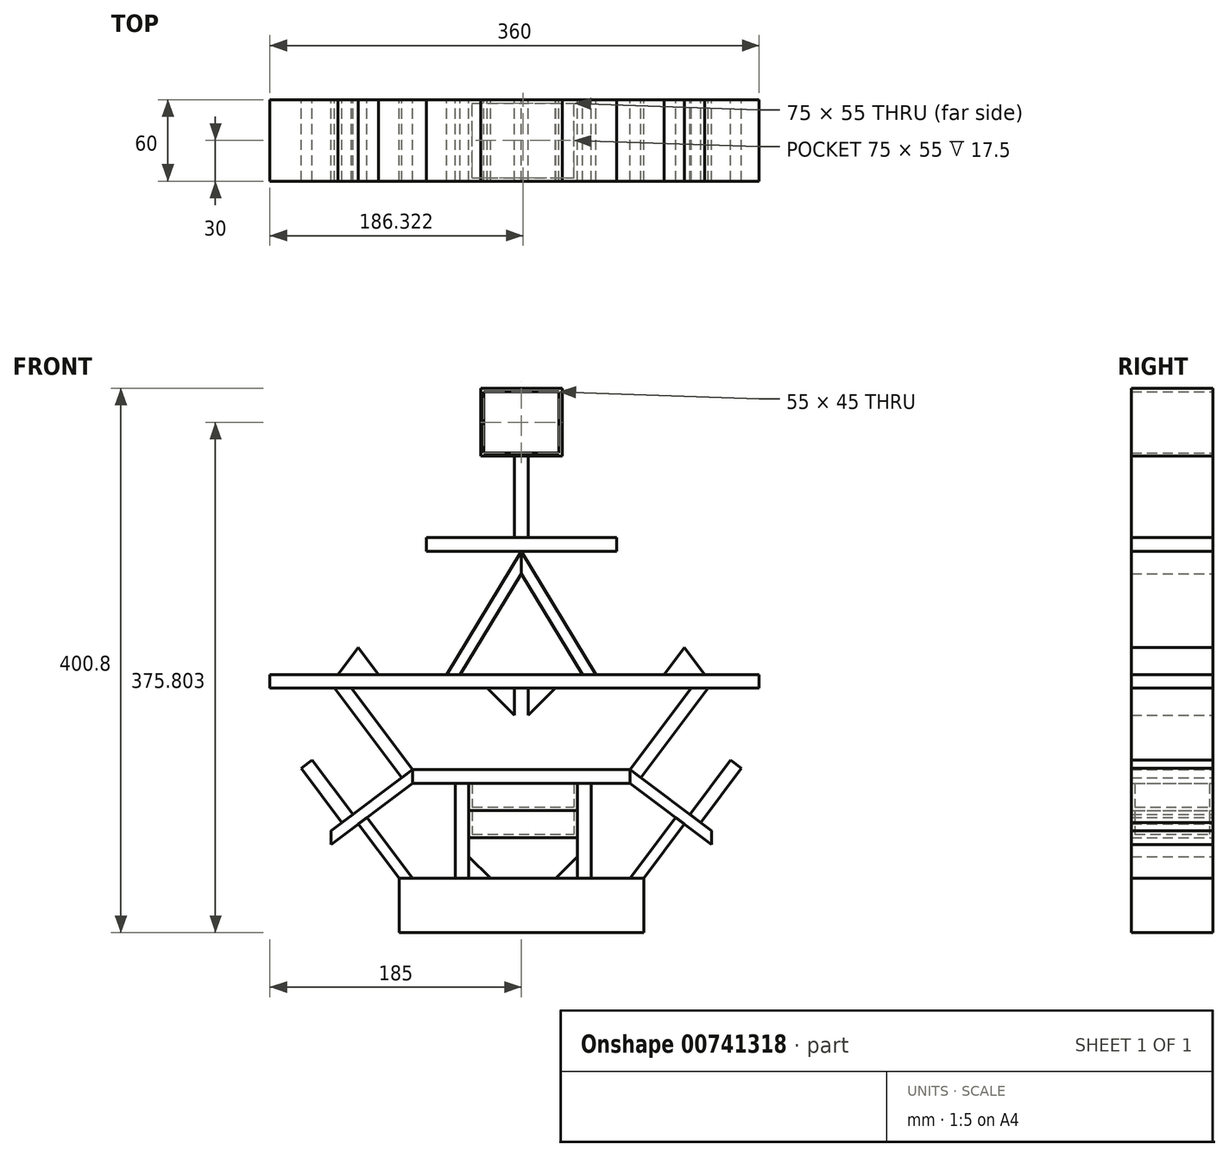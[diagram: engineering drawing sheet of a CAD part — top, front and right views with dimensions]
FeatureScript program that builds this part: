
annotation { "Feature Type Name" : "Feature", "Feature Type Description" : "" }
export const myFeature = defineFeature(function(context is Context, id is Id, definition is map)
    precondition{}
    {
        {
            var Q0;
            Q0=qCreatedBy(makeId("Top.planeOp"),FACE);
            var sketch = newSketch(context, id + "F0", { "sketchPlane" : qUnion([Q0])});
            skLineSegment(sketch, "E0.bottom", {"start": v(90, -30) * mm, "end": v(-90, -30) * mm});
            skLineSegment(sketch, "E0.top", {"start": v(90, 30) * mm, "end": v(-90, 30) * mm});
            skLineSegment(sketch, "E0.left", {"start": v(90, -30) * mm, "end": v(90, 30) * mm});
            skLineSegment(sketch, "E0.right", {"start": v(-90, -30) * mm, "end": v(-90, 30) * mm});
            skPoint(sketch, "E0.middle", {"position": v(0, 0) * mm});
            skSolve(sketch);
        }
        {
            var Q0;
            Q0 = qSketchRegion(id + "F0", true);
            extrude(context, id + "F1", {"entities" : qUnion([Q0]), "oppositeDirection" : true, "depth" : 40 * mm, "offsetDistance" : 25 * mm});
        }
        {
            var Q0;
            Q0=makeQuery(id+"F1.opExtrude","SWEPT_FACE",FACE,{"disambiguationData":[OSD([sQuery(id+"F0.wireOp",EDGE,"E0.top")])]});
            var sketch = newSketch(context, id + "F2", { "sketchPlane" : qUnion([Q0])});
            skLineSegment(sketch, "E1", {"start": v(90, 0) * mm, "end": v(80, 0) * mm});
            skLineSegment(sketch, "E2", {"start": v(80, 0) * mm, "end": v(113.6, 44.8) * mm});
            skLineSegment(sketch, "E3", {"start": v(120, 40) * mm, "end": v(90, 0) * mm});
            skLineSegment(sketch, "E4.bottom", {"start": v(38.68, 70) * mm, "end": v(-41.32, 70) * mm});
            skLineSegment(sketch, "E4.top", {"start": v(38.68, 0) * mm, "end": v(-41.32, 0) * mm});
            skLineSegment(sketch, "E4.left", {"start": v(38.68, 70) * mm, "end": v(38.68, 0) * mm});
            skLineSegment(sketch, "E4.right", {"start": v(-41.32, 70) * mm, "end": v(-41.32, 0) * mm});
            skLineSegment(sketch, "E5", {"start": v(38.68, 30) * mm, "end": v(-41.32, 30) * mm});
            skLineSegment(sketch, "E6", {"start": v(38.68, 50) * mm, "end": v(-41.32, 50) * mm});
            skLineSegment(sketch, "E7", {"start": v(-41.32, 16) * mm, "end": v(-25.32, 0) * mm});
            skLineSegment(sketch, "E8", {"start": v(38.68, 70) * mm, "end": v(48.68, 70) * mm});
            skLineSegment(sketch, "E9", {"start": v(48.68, 70) * mm, "end": v(48.68, 0) * mm});
            skLineSegment(sketch, "E10", {"start": v(-41.32, 70) * mm, "end": v(-51.32, 70) * mm});
            skLineSegment(sketch, "E11", {"start": v(-51.32, 70) * mm, "end": v(-51.32, 0) * mm});
            skLineSegment(sketch, "E12", {"start": v(38.68, 16) * mm, "end": v(22.68, 0) * mm});
            skLineSegment(sketch, "E13", {"start": v(113.6, 44.8) * mm, "end": v(120, 40) * mm});
            skLineSegment(sketch, "E14", {"start": v(80, 70) * mm, "end": v(-80, 70) * mm});
            skLineSegment(sketch, "E15", {"start": v(-80, 70) * mm, "end": v(-80, 80) * mm});
            skLineSegment(sketch, "E16", {"start": v(-80, 80) * mm, "end": v(80, 80) * mm});
            skLineSegment(sketch, "E17", {"start": v(80, 80) * mm, "end": v(80, 70) * mm});
            skLineSegment(sketch, "E18", {"start": v(5, 80) * mm, "end": v(-5, 80) * mm});
            skLineSegment(sketch, "E19", {"start": v(-5, 80) * mm, "end": v(-5, 140) * mm});
            skLineSegment(sketch, "E20", {"start": v(-5, 140) * mm, "end": v(5, 140) * mm});
            skLineSegment(sketch, "E21", {"start": v(5, 140) * mm, "end": v(5, 80) * mm});
            skLineSegment(sketch, "E22", {"start": v(185, 140) * mm, "end": v(-175, 140) * mm});
            skLineSegment(sketch, "E23", {"start": v(-175, 140) * mm, "end": v(-175, 150) * mm});
            skLineSegment(sketch, "E24", {"start": v(-175, 150) * mm, "end": v(185, 150) * mm});
            skLineSegment(sketch, "E25", {"start": v(185, 150) * mm, "end": v(185, 140) * mm});
            skLineSegment(sketch, "E26", {"start": v(80, 80) * mm, "end": v(140, 35) * mm});
            skLineSegment(sketch, "E27", {"start": v(140, 35) * mm, "end": v(140, 25) * mm});
            skLineSegment(sketch, "E28", {"start": v(140, 25) * mm, "end": v(80, 70) * mm});
            skLineSegment(sketch, "E29", {"start": v(124, 47) * mm, "end": v(154, 87) * mm});
            skLineSegment(sketch, "E30", {"start": v(154, 87) * mm, "end": v(162, 81) * mm});
            skLineSegment(sketch, "E31", {"start": v(162, 81) * mm, "end": v(132, 41) * mm});
            skLineSegment(sketch, "E32", {"start": v(80, 80) * mm, "end": v(125, 140) * mm});
            skLineSegment(sketch, "E33", {"start": v(125, 140) * mm, "end": v(137.5, 140) * mm});
            skLineSegment(sketch, "E34", {"start": v(137.5, 140) * mm, "end": v(88, 74) * mm});
            skLineSegment(sketch, "E35", {"start": v(88, 74) * mm, "end": v(80, 80) * mm});
            skLineSegment(sketch, "E36", {"start": v(25, 140) * mm, "end": v(5, 120) * mm});
            skLineSegment(sketch, "E37", {"start": v(25, 140) * mm, "end": v(5, 140) * mm});
            skLineSegment(sketch, "E38", {"start": v(5, 120) * mm, "end": v(5, 140) * mm});
            skLineSegment(sketch, "E39", {"start": v(175, 150) * mm, "end": v(165, 150) * mm});
            skLineSegment(sketch, "E40", {"start": v(165, 150) * mm, "end": v(165, 160) * mm});
            skLineSegment(sketch, "E41", {"start": v(165, 160) * mm, "end": v(175, 160) * mm});
            skLineSegment(sketch, "E42", {"start": v(175, 160) * mm, "end": v(175, 150) * mm});
            skLineSegment(sketch, "E43", {"start": v(135, 150) * mm, "end": v(120, 170) * mm});
            skLineSegment(sketch, "E44", {"start": v(120, 170) * mm, "end": v(105, 150) * mm});
            skLineSegment(sketch, "E45", {"start": v(105, 150) * mm, "end": v(135, 150) * mm});
            skLineSegment(sketch, "E46", {"start": v(173.1, 240.8) * mm, "end": v(105, 150) * mm});
            skLineSegment(sketch, "E47", {"start": v(105, 150) * mm, "end": v(95, 150) * mm});
            skLineSegment(sketch, "E48", {"start": v(55, 150) * mm, "end": v(0, 240.8) * mm});
            skLineSegment(sketch, "E49", {"start": v(0, 240.8) * mm, "end": v(0, 224.3) * mm});
            skLineSegment(sketch, "E50", {"start": v(0, 224.3) * mm, "end": v(45, 150) * mm});
            skLineSegment(sketch, "E51", {"start": v(45, 150) * mm, "end": v(55, 150) * mm});
            skLineSegment(sketch, "E52", {"start": v(120, 150) * mm, "end": v(135, 150) * mm});
            skLineSegment(sketch, "E53", {"start": v(173.1, 240.8) * mm, "end": v(163.1, 240.8) * mm});
            skLineSegment(sketch, "E54", {"start": v(163.1, 240.8) * mm, "end": v(95, 150) * mm});
            skLineSegment(sketch, "E55", {"start": v(0, 224.3) * mm, "end": v(0, 240.8) * mm});
            skLineSegment(sketch, "E56", {"start": v(70, 240.8) * mm, "end": v(-70, 240.8) * mm});
            skLineSegment(sketch, "E57", {"start": v(-70, 240.8) * mm, "end": v(-70, 250.8) * mm});
            skLineSegment(sketch, "E58", {"start": v(-70, 250.8) * mm, "end": v(70, 250.8) * mm});
            skLineSegment(sketch, "E59", {"start": v(70, 250.8) * mm, "end": v(70, 240.8) * mm});
            skLineSegment(sketch, "E60", {"start": v(0, 240.8) * mm, "end": v(10, 224.3) * mm});
            skLineSegment(sketch, "E61", {"start": v(30, 240.8) * mm, "end": v(0, 240.8) * mm});
            skLineSegment(sketch, "E62", {"start": v(30, 240.8) * mm, "end": v(15, 216.67) * mm});
            skLineSegment(sketch, "E63", {"start": v(15, 216.67) * mm, "end": v(0, 240.8) * mm});
            skLineSegment(sketch, "E64", {"start": v(0, 224.3) * mm, "end": v(10.42, 207.09) * mm});
            skLineSegment(sketch, "E65", {"start": v(10.42, 207.09) * mm, "end": v(-10.75, 207.09) * mm});
            skLineSegment(sketch, "E66", {"start": v(-10.75, 207.09) * mm, "end": v(0, 224.3) * mm});
            skLineSegment(sketch, "E67", {"start": v(70, 250.8) * mm, "end": v(60, 250.8) * mm});
            skLineSegment(sketch, "E68", {"start": v(60, 250.8) * mm, "end": v(60, 290.8) * mm});
            skLineSegment(sketch, "E69", {"start": v(60, 290.8) * mm, "end": v(70, 290.8) * mm});
            skLineSegment(sketch, "E70", {"start": v(70, 290.8) * mm, "end": v(70, 250.8) * mm});
            skLineSegment(sketch, "E71", {"start": v(15, 250.8) * mm, "end": v(0, 250.8) * mm});
            skLineSegment(sketch, "E72", {"start": v(5, 310.8) * mm, "end": v(-5, 310.8) * mm});
            skLineSegment(sketch, "E73", {"start": v(-5, 310.8) * mm, "end": v(-5, 250.8) * mm});
            skLineSegment(sketch, "E74", {"start": v(5, 310.8) * mm, "end": v(5, 250.8) * mm});
            skLineSegment(sketch, "E75", {"start": v(5, 250.8) * mm, "end": v(-5, 250.8) * mm});
            skLineSegment(sketch, "E76", {"start": v(-30, 310.8) * mm, "end": v(-30, 360.8) * mm});
            skLineSegment(sketch, "E77", {"start": v(-30, 360.8) * mm, "end": v(30, 360.8) * mm});
            skLineSegment(sketch, "E78", {"start": v(30, 360.8) * mm, "end": v(30, 310.8) * mm});
            skLineSegment(sketch, "E79", {"start": v(30, 310.8) * mm, "end": v(-30, 310.8) * mm});
            skSolve(sketch);
        }
        {
            var Q0;
            Q0=makeQuery(id+"F2.imprint","IMPRINT",FACE,{"disambiguationData":[TD([[makeQuery(id+"F2.imprint","IMPRINT",EDGE,{"derivedFrom":sQuery(id+"F2.wireOp",EDGE,"E1")}),1.0]])]});
            var Q1;
            {var subQ0=sQuery(id+"F2.wireOp",EDGE,"E29");Q1=makeQuery(id+"F2.imprint","IMPRINT",FACE,{"disambiguationData":[TD([[makeQuery(id+"F2.imprint","IMPRINT",EDGE,{"derivedFrom":subQ0}),-1.0]])]});}
            var Q2;
            Q2=makeQuery(id+"F2.imprint","IMPRINT",FACE,{"disambiguationData":[TD([[makeQuery(id+"F2.imprint","IMPRINT",EDGE,{"derivedFrom":sQuery(id+"F2.wireOp",EDGE,"E32")}),-1.0]])]});
            var Q3;
            Q3=makeQuery(id+"F2.imprint","IMPRINT",FACE,{"disambiguationData":[TD([[makeQuery(id+"F2.imprint","IMPRINT",EDGE,{"derivedFrom":sQuery(id+"F2.wireOp",EDGE,"E36")}),-1.0]])]});
            var Q4;
            Q4=makeQuery(id+"F2.imprint","IMPRINT",FACE,{"disambiguationData":[TD([[makeQuery(id+"F2.imprint","IMPRINT",EDGE,{"derivedFrom":sQuery(id+"F2.wireOp",EDGE,"E43")}),1.0]])]});
            var Q5;
            Q5=makeQuery(id+"F2.imprint","IMPRINT",FACE,{"disambiguationData":[TD([[makeQuery(id+"F2.imprint","IMPRINT",EDGE,{"derivedFrom":sQuery(id+"F2.wireOp",EDGE,"E39")}),-1.0]])]});
            var Q6;
            Q6=makeQuery(id+"F2.imprint","IMPRINT",FACE,{"disambiguationData":[TD([[makeQuery(id+"F2.imprint","IMPRINT",EDGE,{"derivedFrom":sQuery(id+"F2.wireOp",EDGE,"E48")}),1.0]])]});
            var Q7;
            Q7=sQuery(id+"F2.wireOp",EDGE,"y02XFMRa-m6S5-seBa-FdlV-A9luelnOKwn0");
            var Q8;
            Q8=sQuery(id+"F2.wireOp",EDGE,"E3");
            var Q9;
            Q9=sQuery(id+"F2.wireOp",EDGE,"E2");
            var Q10;
            Q10=sQuery(id+"F2.wireOp",EDGE,"E1");
            extrude(context, id + "F3", {"entities" : qUnion([Q0, Q1, Q2, Q3, Q4, Q5, Q6]), "surfaceEntities" : qUnion([Q7, Q8, Q9, Q10]), "oppositeDirection" : true, "depth" : 60 * mm, "offsetDistance" : 25 * mm});
        }
        {
            var Q0;
            Q0=makeQuery(id+"F3.opExtrude","SWEPT_BODY",BODY,{"disambiguationData":[OSD([sQuery(id+"F2.wireOp",EDGE,"E2")])]});
            var Q1;
            Q1=makeQuery(id+"F3.opExtrude","SWEPT_BODY",BODY,{"disambiguationData":[OSD([sQuery(id+"F2.wireOp",EDGE,"E26"),sQuery(id+"F2.wireOp",EDGE,"E29"),sQuery(id+"F2.wireOp",EDGE,"E30"),sQuery(id+"F2.wireOp",EDGE,"E31")])]});
            var Q2;
            Q2=makeQuery(id+"F3.opExtrude","SWEPT_BODY",BODY,{"disambiguationData":[OSD([sQuery(id+"F2.wireOp",EDGE,"E32"),sQuery(id+"F2.wireOp",EDGE,"E33"),sQuery(id+"F2.wireOp",EDGE,"E34"),sQuery(id+"F2.wireOp",EDGE,"E35")])]});
            var Q3;
            Q3=makeQuery(id+"F3.opExtrude","SWEPT_BODY",BODY,{"disambiguationData":[OSD([sQuery(id+"F2.wireOp",EDGE,"E36"),sQuery(id+"F2.wireOp",EDGE,"E38"),sQuery(id+"F2.wireOp",EDGE,"E37")])]});
            var Q4;
            Q4=makeQuery(id+"F3.opExtrude","SWEPT_BODY",BODY,{"disambiguationData":[OSD([sQuery(id+"F2.wireOp",EDGE,"E39"),sQuery(id+"F2.wireOp",EDGE,"E40"),sQuery(id+"F2.wireOp",EDGE,"E41"),sQuery(id+"F2.wireOp",EDGE,"E42")])]});
            var Q5;
            Q5=makeQuery(id+"F3.opExtrude","SWEPT_BODY",BODY,{"disambiguationData":[OSD([sQuery(id+"F2.wireOp",EDGE,"E43"),sQuery(id+"F2.wireOp",EDGE,"E44"),sQuery(id+"F2.wireOp",EDGE,"E45"),sQuery(id+"F2.wireOp",EDGE,"E52")])]});
            var Q6;
            Q6=makeQuery(id+"F3.opExtrude","SWEPT_BODY",BODY,{"disambiguationData":[OSD([sQuery(id+"F2.wireOp",EDGE,"E48"),sQuery(id+"F2.wireOp",EDGE,"E50"),sQuery(id+"F2.wireOp",EDGE,"E51"),sQuery(id+"F2.wireOp",EDGE,"E55")])]});
            var Q7;
            Q7=qCreatedBy(makeId("Right.planeOp"),FACE);
            mirror(context, id + "F4", {"entities" : qUnion([Q0, Q1, Q2, Q3, Q4, Q5, Q6]), "mirrorPlane" : qUnion([Q7])});
        }
        {
            var Q0;
            {var subQ0=sQuery(id+"F2.wireOp",EDGE,"E5");Q0=makeQuery(id+"F2.imprint","IMPRINT",FACE,{"disambiguationData":[TD([[makeQuery(id+"F2.imprint","IMPRINT",EDGE,{"derivedFrom":subQ0}),-1.0]])]});}
            extrude(context, id + "F5", {"entities" : qUnion([Q0]), "oppositeDirection" : true, "depth" : 60 * mm, "offsetDistance" : 25 * mm});
        }
        {
            var Q0;
            Q0=makeQuery(id+"F5.opExtrude","SWEPT_FACE",FACE,{"disambiguationData":[OSD([sQuery(id+"F2.wireOp",EDGE,"E6")])]});
            shell(context, id + "F6", {"entities" : qUnion([Q0]), "thickness" : 2.5 * mm});
        }
        {
            var Q0;
            {var subQ0=sQuery(id+"F2.wireOp",EDGE,"E4.bottom");Q0=makeQuery(id+"F2.imprint","IMPRINT",FACE,{"disambiguationData":[TD([[makeQuery(id+"F2.imprint","IMPRINT",EDGE,{"derivedFrom":subQ0}),1.0]])]});}
            var Q1;
            {var subQ3=sQuery(id+"F2.wireOp",EDGE,"E6");Q1=makeQuery(id+"F2.imprint","IMPRINT",FACE,{"disambiguationData":[TD([[makeQuery(id+"F2.imprint","IMPRINT",EDGE,{"derivedFrom":subQ3}),-1.0]])]});}
            var Q2;
            Q2=makeQuery(id+"F2.imprint","IMPRINT",FACE,{"disambiguationData":[TD([[makeQuery(id+"F2.imprint","IMPRINT",EDGE,{"derivedFrom":sQuery(id+"F2.wireOp",EDGE,"E64")}),-1.0]])]});
            extrude(context, id + "F7", {"entities" : qUnion([Q0, Q1, Q2]), "oppositeDirection" : true, "depth" : 60 * mm, "offsetDistance" : 25 * mm});
        }
        {
            var Q0;
            Q0=makeQuery(id+"F7.opExtrude","SWEPT_FACE",FACE,{"disambiguationData":[OSD([sQuery(id+"F2.wireOp",EDGE,"E4.bottom")])]});
            var Q1;
            Q1=makeQuery(id+"F7.opExtrude","SWEPT_FACE",FACE,{"disambiguationData":[OSD([sQuery(id+"F2.wireOp",EDGE,"E14")])]});
            shell(context, id + "F8", {"entities" : qUnion([Q0, Q1]), "thickness" : 2.5 * mm});
        }
        {
            var Q0;
            {var subQ8=sQuery(id+"F2.wireOp",EDGE,"E9");Q0=makeQuery(id+"F2.imprint","IMPRINT",FACE,{"disambiguationData":[TD([[makeQuery(id+"F2.imprint","IMPRINT",EDGE,{"derivedFrom":subQ8}),-1.0]])]});}
            var Q1;
            {var subQ6=sQuery(id+"F2.wireOp",EDGE,"E11");Q1=makeQuery(id+"F2.imprint","IMPRINT",FACE,{"disambiguationData":[TD([[makeQuery(id+"F2.imprint","IMPRINT",EDGE,{"derivedFrom":subQ6}),1.0]])]});}
            var Q2;
            Q2=makeQuery(id+"F2.imprint","IMPRINT",FACE,{"disambiguationData":[TD([[makeQuery(id+"F2.imprint","IMPRINT",EDGE,{"derivedFrom":sQuery(id+"F2.wireOp",EDGE,"E18")}),-1.0]])]});
            extrude(context, id + "F9", {"entities" : qUnion([Q0, Q1, Q2]), "oppositeDirection" : true, "depth" : 60 * mm, "offsetDistance" : 25 * mm});
        }
        {
            var Q0;
            {var subQ3=sQuery(id+"F2.wireOp",EDGE,"E7");Q0=makeQuery(id+"F2.imprint","IMPRINT",FACE,{"disambiguationData":[TD([[makeQuery(id+"F2.imprint","IMPRINT",EDGE,{"derivedFrom":subQ3}),-1.0]])]});}
            var Q1;
            {var subQ3=sQuery(id+"F2.wireOp",EDGE,"E12");Q1=makeQuery(id+"F2.imprint","IMPRINT",FACE,{"disambiguationData":[TD([[makeQuery(id+"F2.imprint","IMPRINT",EDGE,{"derivedFrom":subQ3}),1.0]])]});}
            var Q2;
            {var subQ0=sQuery(id+"F2.wireOp",EDGE,"E23");Q2=makeQuery(id+"F2.imprint","IMPRINT",FACE,{"disambiguationData":[TD([[makeQuery(id+"F2.imprint","IMPRINT",EDGE,{"derivedFrom":subQ0}),-1.0]])]});}
            var Q3;
            {var subQ6=sQuery(id+"F2.wireOp",EDGE,"E15");Q3=makeQuery(id+"F2.imprint","IMPRINT",FACE,{"disambiguationData":[TD([[makeQuery(id+"F2.imprint","IMPRINT",EDGE,{"derivedFrom":subQ6}),-1.0]])]});}
            var Q4;
            Q4=makeQuery(id+"F2.imprint","IMPRINT",FACE,{"disambiguationData":[TD([[makeQuery(id+"F2.imprint","IMPRINT",EDGE,{"derivedFrom":sQuery(id+"F2.wireOp",EDGE,"E61")}),1.0]])]});
            extrude(context, id + "F10", {"entities" : qUnion([Q0, Q1, Q2, Q3, Q4]), "oppositeDirection" : true, "depth" : 60 * mm, "offsetDistance" : 25 * mm});
        }
        {
            var Q0;
            {var subQ6=sQuery(id+"F2.wireOp",EDGE,"E15");Q0=makeQuery(id+"F2.imprint","IMPRINT",FACE,{"disambiguationData":[TD([[makeQuery(id+"F2.imprint","IMPRINT",EDGE,{"derivedFrom":subQ6}),-1.0]])]});}
            var Q1;
            {var subQ0=sQuery(id+"F2.wireOp",EDGE,"E57");Q1=makeQuery(id+"F2.imprint","IMPRINT",FACE,{"disambiguationData":[TD([[makeQuery(id+"F2.imprint","IMPRINT",EDGE,{"derivedFrom":subQ0}),-1.0]])]});}
            extrude(context, id + "F11", {"entities" : qUnion([Q0, Q1]), "oppositeDirection" : true, "depth" : 60 * mm, "offsetDistance" : 25 * mm});
        }
        {
            var Q0;
            {var subQ3=sQuery(id+"F2.wireOp",EDGE,"E17");Q0=makeQuery(id+"F2.imprint","IMPRINT",FACE,{"disambiguationData":[TD([[makeQuery(id+"F2.imprint","IMPRINT",EDGE,{"derivedFrom":subQ3}),1.0]])]});}
            var Q1;
            {var subQ1=sQuery(id+"F2.wireOp",EDGE,"E47");Q1=makeQuery(id+"F2.imprint","IMPRINT",FACE,{"disambiguationData":[TD([[makeQuery(id+"F2.imprint","IMPRINT",EDGE,{"derivedFrom":subQ1}),-1.0]])]});}
            var Q2;
            Q2=makeQuery(id+"F2.imprint","IMPRINT",FACE,{"disambiguationData":[TD([[makeQuery(id+"F2.imprint","IMPRINT",EDGE,{"derivedFrom":sQuery(id+"F2.wireOp",EDGE,"E67")}),-1.0]])]});
            var Q3;
            Q3=makeQuery(id+"F2.imprint","IMPRINT",FACE,{"disambiguationData":[TD([[makeQuery(id+"F2.imprint","IMPRINT",EDGE,{"derivedFrom":sQuery(id+"F2.wireOp",EDGE,"E72")}),1.0]])]});
            var Q4;
            {var subQ1=sQuery(id+"F2.wireOp",EDGE,"E73");Q4=makeQuery(id+"F2.imprint","IMPRINT",FACE,{"disambiguationData":[TD([[makeQuery(id+"F2.imprint","IMPRINT",EDGE,{"derivedFrom":subQ1}),1.0]])]});}
            extrude(context, id + "F12", {"entities" : qUnion([Q0, Q1, Q2, Q3, Q4]), "oppositeDirection" : true, "depth" : 60 * mm, "offsetDistance" : 25 * mm});
        }
        {
            var Q0;
            Q0=makeQuery(id+"F12.opExtrude","SWEPT_BODY",BODY,{"disambiguationData":[OSD([sQuery(id+"F2.wireOp",EDGE,"E17"),sQuery(id+"F2.wireOp",EDGE,"E26"),sQuery(id+"F2.wireOp",EDGE,"E27"),sQuery(id+"F2.wireOp",EDGE,"E28")])]});
            var Q1;
            Q1=makeQuery(id+"F12.opExtrude","SWEPT_BODY",BODY,{"disambiguationData":[OSD([sQuery(id+"F2.wireOp",EDGE,"E46"),sQuery(id+"F2.wireOp",EDGE,"E47"),sQuery(id+"F2.wireOp",EDGE,"E53"),sQuery(id+"F2.wireOp",EDGE,"E54")])]});
            var Q2;
            Q2=makeQuery(id+"F10.opExtrude","SWEPT_BODY",BODY,{"disambiguationData":[OSD([sQuery(id+"F2.wireOp",EDGE,"E61"),sQuery(id+"F2.wireOp",EDGE,"SDPe51lW-uxlw-PNV4-2gwS-GSvddlQauJM2"),sQuery(id+"F2.wireOp",EDGE,"E62"),sQuery(id+"F2.wireOp",EDGE,"E63")])]});
            var Q3;
            Q3=makeQuery(id+"F12.opExtrude","SWEPT_BODY",BODY,{"disambiguationData":[OSD([sQuery(id+"F2.wireOp",EDGE,"E67"),sQuery(id+"F2.wireOp",EDGE,"E68"),sQuery(id+"F2.wireOp",EDGE,"E69"),sQuery(id+"F2.wireOp",EDGE,"E70")])]});
            var Q4;
            Q4=qCreatedBy(makeId("Right.planeOp"),FACE);
            mirror(context, id + "F13", {"entities" : qUnion([Q0, Q1, Q2, Q3]), "mirrorPlane" : qUnion([Q4])});
        }
        {
            var Q0;
            {var subQ3=sQuery(id+"F2.wireOp",EDGE,"E76");Q0=makeQuery(id+"F2.imprint","IMPRINT",FACE,{"disambiguationData":[TD([[makeQuery(id+"F2.imprint","IMPRINT",EDGE,{"derivedFrom":subQ3}),-1.0]])]});}
            extrude(context, id + "F14", {"entities" : qUnion([Q0]), "oppositeDirection" : true, "depth" : 60 * mm, "offsetDistance" : 25 * mm});
        }
        {
            var Q0;
            Q0=makeQuery(id+"F14.opExtrude","CAP_FACE",FACE,{"disambiguationData":[OSD([sQuery(id+"F2.wireOp",EDGE,"E76"),sQuery(id+"F2.wireOp",EDGE,"E77"),sQuery(id+"F2.wireOp",EDGE,"E78"),sQuery(id+"F2.wireOp",EDGE,"E79")])],"isStart":false});
            var Q1;
            Q1=makeQuery(id+"F14.opExtrude","CAP_FACE",FACE,{"disambiguationData":[OSD([sQuery(id+"F2.wireOp",EDGE,"E76"),sQuery(id+"F2.wireOp",EDGE,"E77"),sQuery(id+"F2.wireOp",EDGE,"E78"),sQuery(id+"F2.wireOp",EDGE,"E79")])],"isStart":true});
            shell(context, id + "F15", {"entities" : qUnion([Q0, Q1]), "thickness" : 2.5 * mm});
        }
    });
